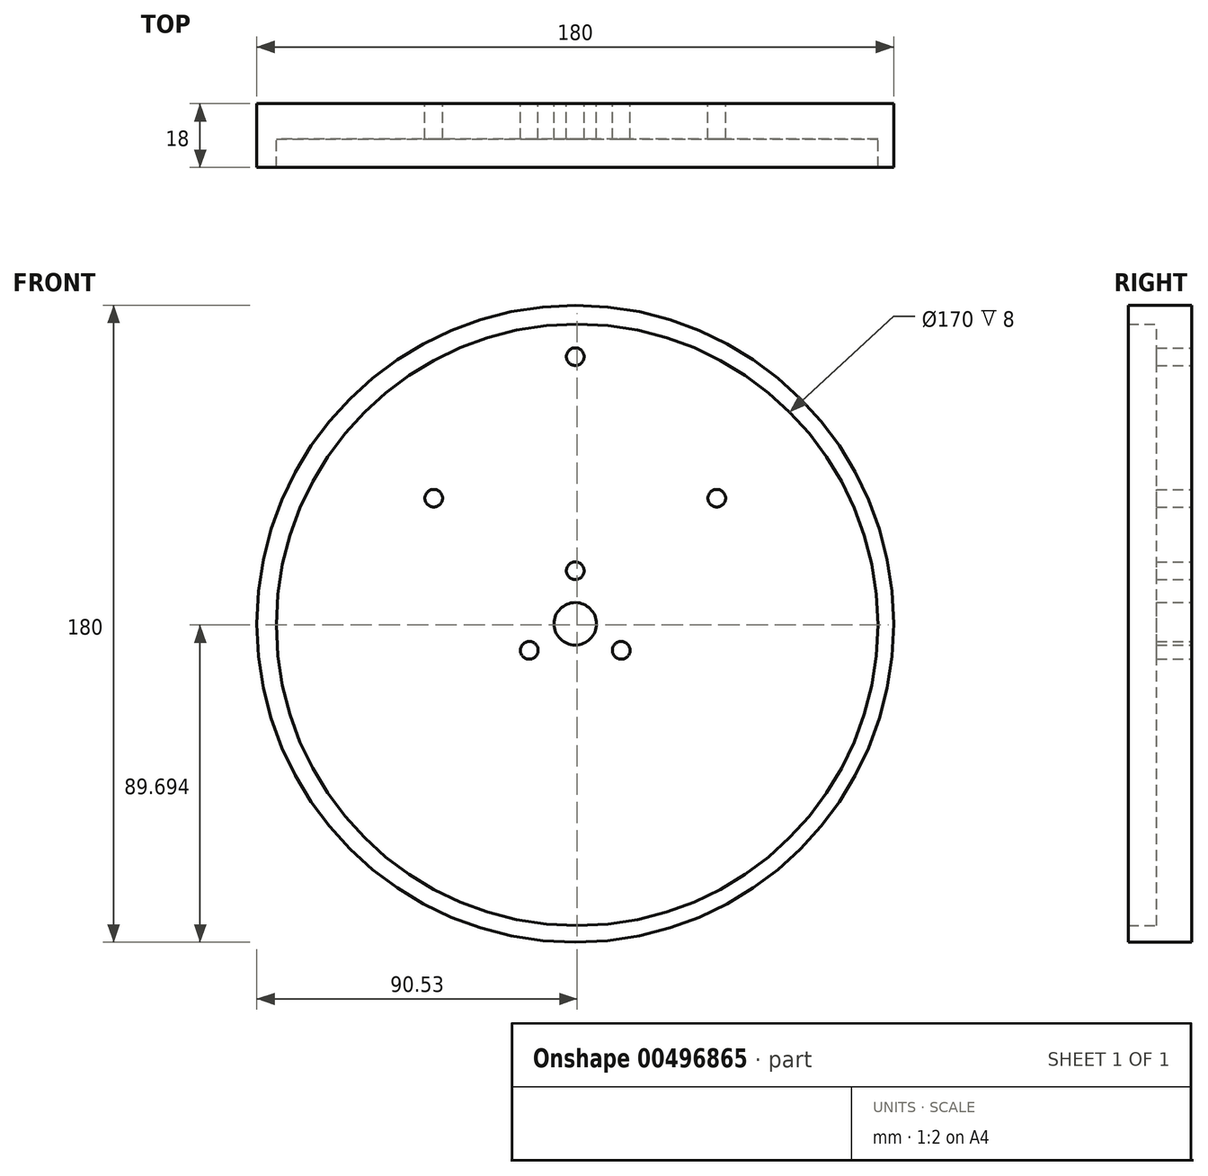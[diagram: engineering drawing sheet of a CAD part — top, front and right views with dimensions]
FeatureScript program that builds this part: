
annotation { "Feature Type Name" : "Feature", "Feature Type Description" : "" }
export const myFeature = defineFeature(function(context is Context, id is Id, definition is map)
    precondition{}
    {
        {
            var Q0;
            Q0=qCreatedBy(makeId("Front.planeOp"),FACE);
            var sketch = newSketch(context, id + "F0", { "sketchPlane" : qUnion([Q0])});
            skCircle(sketch, "E0", {"center": v(0, 0) * mm, "radius": 6 * mm});
            skCircle(sketch, "E1", {"center": v(0, 0) * mm, "radius": 90 * mm});
            skCircle(sketch, "E2", {"center": v(0, 15) * mm, "radius": 2.5 * mm});
            skCircle(sketch, "E3", {"center": v(-13, -7.5) * mm, "radius": 2.5 * mm});
            skCircle(sketch, "E4", {"center": v(13, -7.5) * mm, "radius": 2.5 * mm});
            skCircle(sketch, "E5", {"center": v(0.53, -0.3) * mm, "radius": 85 * mm});
            skCircle(sketch, "E6", {"center": v(-40, 35.5) * mm, "radius": 2.5 * mm});
            skCircle(sketch, "E7", {"center": v(40, 35.5) * mm, "radius": 2.5 * mm});
            skCircle(sketch, "E8", {"center": v(0, 75.5) * mm, "radius": 2.5 * mm});
            skSolve(sketch);
        }
        {
            var Q0;
            Q0=makeQuery(id+"F0.imprint","IMPRINT",FACE,{"disambiguationData":[TD([[makeQuery(id+"F0.imprint","IMPRINT",EDGE,{"derivedFrom":sQuery(id+"F0.wireOp",EDGE,"E6")}),-1.0]])]});
            extrude(context, id + "F1", {"entities" : qUnion([Q0]), "depth" : 5 * mm});
        }
        {
            var Q0;
            Q0=makeQuery(id+"F0.imprint","IMPRINT",FACE,{"disambiguationData":[TD([[makeQuery(id+"F0.imprint","IMPRINT",EDGE,{"derivedFrom":sQuery(id+"F0.wireOp",EDGE,"E1")}),1.0]])]});
            extrude(context, id + "F2", {"entities" : qUnion([Q0]), "operationType" : NewBodyOperationType.ADD, "depth" : 18 * mm});
        }
        {
            var Q0;
            Q0=makeQuery(id+"F0.imprint","IMPRINT",FACE,{"disambiguationData":[TD([[makeQuery(id+"F0.imprint","IMPRINT",EDGE,{"derivedFrom":sQuery(id+"F0.wireOp",EDGE,"E2")}),-1.0]])]});
            extrude(context, id + "F3", {"entities" : qUnion([Q0]), "operationType" : NewBodyOperationType.ADD, "depth" : 10 * mm});
        }
    });
